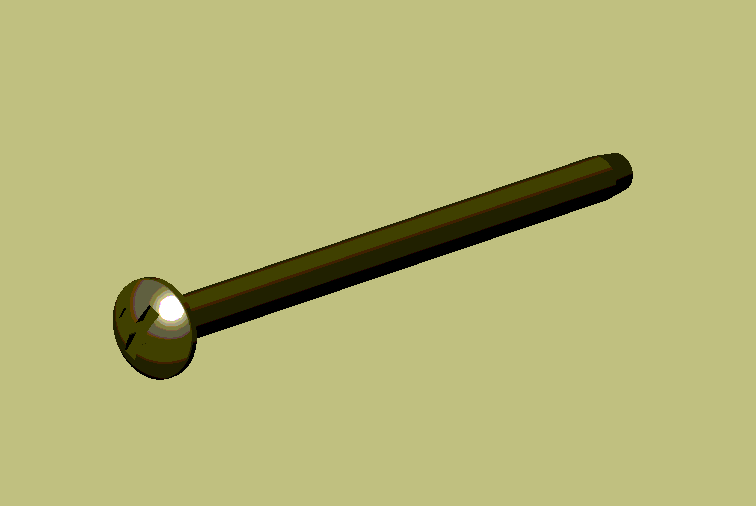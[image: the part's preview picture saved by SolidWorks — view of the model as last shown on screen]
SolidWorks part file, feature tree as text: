
SOLIDWORKS PART (.sldprt)
format: sldprt  version: not decoded by parser v0  size: 145,920 bytes
history: native  units: mm
features: plane x4, sketch x4, fillet x2, material x1, revolve x1, extrude x1, chamfer x1, cut_extrude x1 (+8 scaffold rows collapsed)
feature tree (23):
  scaffold x8  (default folders/planes/origin — collapsed)
  material  "Matériau <non spécifié>"
  plane  "Plane1"
  plane  "Plane2"
  plane  "Plane3"
  sketch  "Esquisse1"  dims[D1=9.0mm D2=32.0mm D3=3.0mm]
  revolve  "Base-Révolution"  Angle=360deg
  sketch  "Esquisse2"
  extrude  "Boss.-Extru.1"  Depth=0.5mm
  fillet  "Congé1"  Radius=0.25mm
  sketch  "Esquisse3"  dims[D1=3.0mm]
  fillet  "Boss.-Extru.2"  Radius=46mm
  chamfer  "Chanfrein1"  Distance=2mm
  plane  "Plan1"  Offset=3mm
  sketch  "Esquisse4"  dims[D3=1.5mm D1=1.0mm D2=2.0mm]
  cut_extrude  "Enlèv. mat.-Extru.2"  Depth=1.75mm
decode coverage: 9 of 10 modeling features carry decoded parameters
note: suppression state not decoded; provenance and decode notes live in map.json
